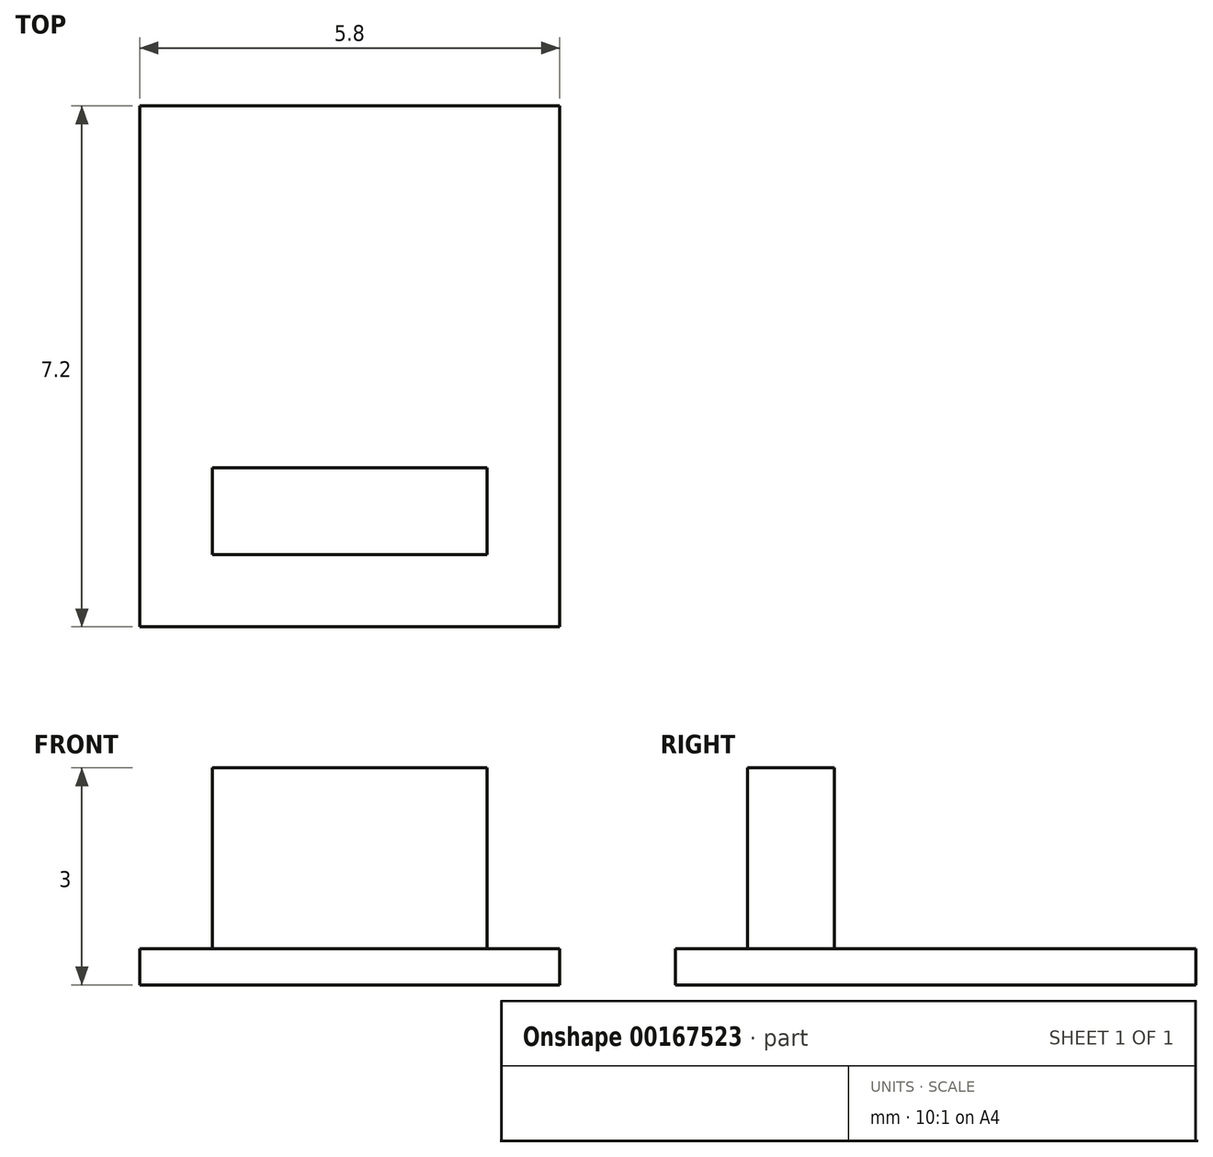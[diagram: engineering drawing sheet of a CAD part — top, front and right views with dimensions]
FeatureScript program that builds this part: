
annotation { "Feature Type Name" : "Feature", "Feature Type Description" : "" }
export const myFeature = defineFeature(function(context is Context, id is Id, definition is map)
    precondition{}
    {
        {
            var Q0;
            Q0=qCreatedBy(makeId("Top.planeOp"),FACE);
            var sketch = newSketch(context, id + "F0", { "sketchPlane" : qUnion([Q0])});
            skLineSegment(sketch, "E0.bottom", {"start": v(0, 0) * mm, "end": v(3.8, 0) * mm});
            skLineSegment(sketch, "E0.top", {"start": v(0, -1.2) * mm, "end": v(3.8, -1.2) * mm});
            skLineSegment(sketch, "E0.left", {"start": v(0, 0) * mm, "end": v(0, -1.2) * mm});
            skLineSegment(sketch, "E0.right", {"start": v(3.8, 0) * mm, "end": v(3.8, -1.2) * mm});
            skLineSegment(sketch, "E1.bottom", {"start": v(-1, 5) * mm, "end": v(4.8, 5) * mm});
            skLineSegment(sketch, "E1.top", {"start": v(-1, -2.2) * mm, "end": v(4.8, -2.2) * mm});
            skLineSegment(sketch, "E1.left", {"start": v(-1, 5) * mm, "end": v(-1, -2.2) * mm});
            skLineSegment(sketch, "E1.right", {"start": v(4.8, 5) * mm, "end": v(4.8, -2.2) * mm});
            skSolve(sketch);
        }
        {
            var Q0;
            Q0=makeQuery(id+"F0.imprint","IMPRINT",FACE,{"disambiguationData":[TD([[makeQuery(id+"F0.imprint","IMPRINT",EDGE,{"derivedFrom":sQuery(id+"F0.wireOp",EDGE,"E0.bottom")}),-1.0]])]});
            extrude(context, id + "F1", {"entities" : qUnion([Q0]), "depth" : 2.5 * mm});
        }
        {
            var Q0;
            Q0=makeQuery(id+"F0.imprint","IMPRINT",FACE,{"disambiguationData":[TD([[makeQuery(id+"F0.imprint","IMPRINT",EDGE,{"derivedFrom":sQuery(id+"F0.wireOp",EDGE,"E0.bottom")}),1.0]])]});
            var Q1;
            Q1=makeQuery(id+"F0.imprint","IMPRINT",FACE,{"disambiguationData":[TD([[makeQuery(id+"F0.imprint","IMPRINT",EDGE,{"derivedFrom":sQuery(id+"F0.wireOp",EDGE,"E0.bottom")}),-1.0]])]});
            extrude(context, id + "F2", {"entities" : qUnion([Q0, Q1]), "operationType" : NewBodyOperationType.ADD, "oppositeDirection" : true, "depth" : .5 * mm});
        }
    });
